# Revit family: Zumtobel PANOS EVO Q100L 18W LED840 LDO AL WH
name_source: partatom
category: Lighting Fixtures
revit_build: Autodesk Revit 2016 (Build: 20150220_1215(x64)
units: mm (PartAtom-declared; Revit-internal decimal feet)

## family parameters
Cut with Voids When Loaded = No
Host = Face
Light Source = Yes
OmniClass Number = 23.80.70.11
OmniClass Title = Luminaries for Internal Lighting
Part Type = Normal
Room Calculation Point = No
Round Connector Dimension = Use Diameter
Shared = No

## types (1)
- PANOS EVO Q100L 18W LED840
    Apparent Load = 18 VA
    Assembly Code = D5020200
    Body = Zumtobel_Metal_White
    Color Filter = 16777215
    Default Elevation = 0 mm  [stored 0 ft]
    Description = LED ceiling-recessed luminaire
    Dimming Lamp Color Temperature Shift = <None>
    Emit Shape Visible in Rendering = Yes
    Emit from Circle Diameter = 115 mm  [stored 0.377297 ft]
    Height = 100 mm  [stored 0.328084 ft]
    Lamp = LED
    Length = 115 mm  [stored 0.377297 ft]
    Manufacturer = Zumtobel Lighting
    Model = 62907040
    Opening Height = 110 mm  [stored 0.360892 ft]
    Photometric Web File = ST7700.IES
    Reflector = Zumtobel_Metal_White_Self_Illumination
    Tilt Angle = -90.00°
    URL = http://www.zumtobel.com
    Voltage = 230 V
    Width = 115 mm  [stored 0.377297 ft]

note: [stored X ft] marks values corroborated as IEEE doubles in the binary element streams (Revit-internal decimal feet)

## geometry (parser evidence)
native form markers: Sweep x2
no freeform markers — native parametric forms only
